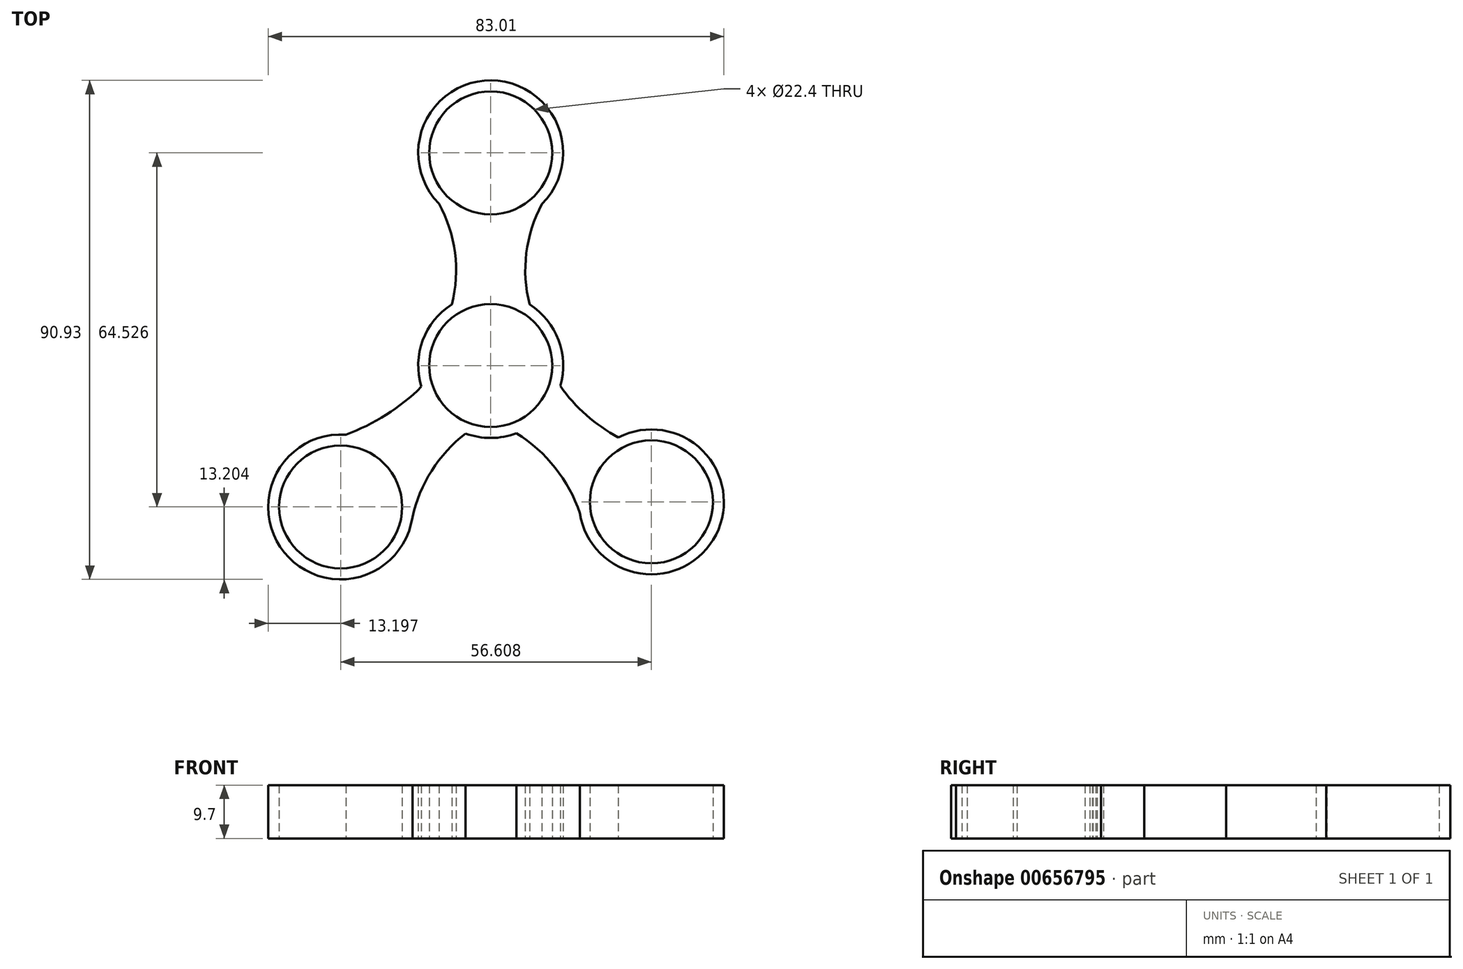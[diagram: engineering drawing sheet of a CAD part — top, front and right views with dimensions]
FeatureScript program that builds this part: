
annotation { "Feature Type Name" : "Feature", "Feature Type Description" : "" }
export const myFeature = defineFeature(function(context is Context, id is Id, definition is map)
    precondition{}
    {
        {
            var Q0;
            Q0=qCreatedBy(makeId("Top.planeOp"),FACE);
            var sketch = newSketch(context, id + "F0", { "sketchPlane" : qUnion([Q0])});
            skCircle(sketch, "E0", {"center": v(0, 0) * mm, "radius": 13.2 * mm});
            skCircle(sketch, "E1", {"center": v(0, 0) * mm, "radius": 11.2 * mm});
            skCircle(sketch, "E2", {"center": v(0, 38.76) * mm, "radius": 13.2 * mm});
            skCircle(sketch, "E3", {"center": v(0, 38.76) * mm, "radius": 11.2 * mm});
            skCircle(sketch, "E4", {"center": v(29.28, -24.84) * mm, "radius": 13.2 * mm});
            skCircle(sketch, "E5", {"center": v(29.28, -24.84) * mm, "radius": 11.2 * mm});
            skCircle(sketch, "E6", {"center": v(-27.33, -25.77) * mm, "radius": 13.2 * mm});
            skCircle(sketch, "E7", {"center": v(-27.33, -25.77) * mm, "radius": 11.2 * mm});
            skArc(sketch, "E8", {"start": v(-13.2, 0) * mm, "mid": v(-6.5, 14.15) * mm, "end": v(-9.44, 29.53) * mm});
            skArc(sketch, "E9", {"start": v(9.32, 29.41) * mm, "mid": v(6.52, 14.08) * mm, "end": v(13.2, 0) * mm});
            skArc(sketch, "E10", {"start": v(7.08, 11.14) * mm, "mid": v(12.15, -3) * mm, "end": v(23.26, -13.1) * mm});
            skArc(sketch, "E11", {"start": v(17.05, -29.8) * mm, "mid": v(7.2, -14.1) * mm, "end": v(-10.35, -8.2) * mm});
            skArc(sketch, "E12", {"start": v(11.34, -6.76) * mm, "mid": v(-5.09, -12.77) * mm, "end": v(-14.27, -27.66) * mm});
            skArc(sketch, "E13", {"start": v(-34.3, -14.56) * mm, "mid": v(-14.44, -5.54) * mm, "end": v(-2.78, 12.9) * mm});
            skSolve(sketch);
        }
        {
            var Q0;
            Q0 = qSketchRegion(id + "F0", true);
            extrude(context, id + "F1", {"entities" : qUnion([Q0]), "depth" : 9.7 * mm, "offsetDistance" : 25 * mm});
        }
    });
